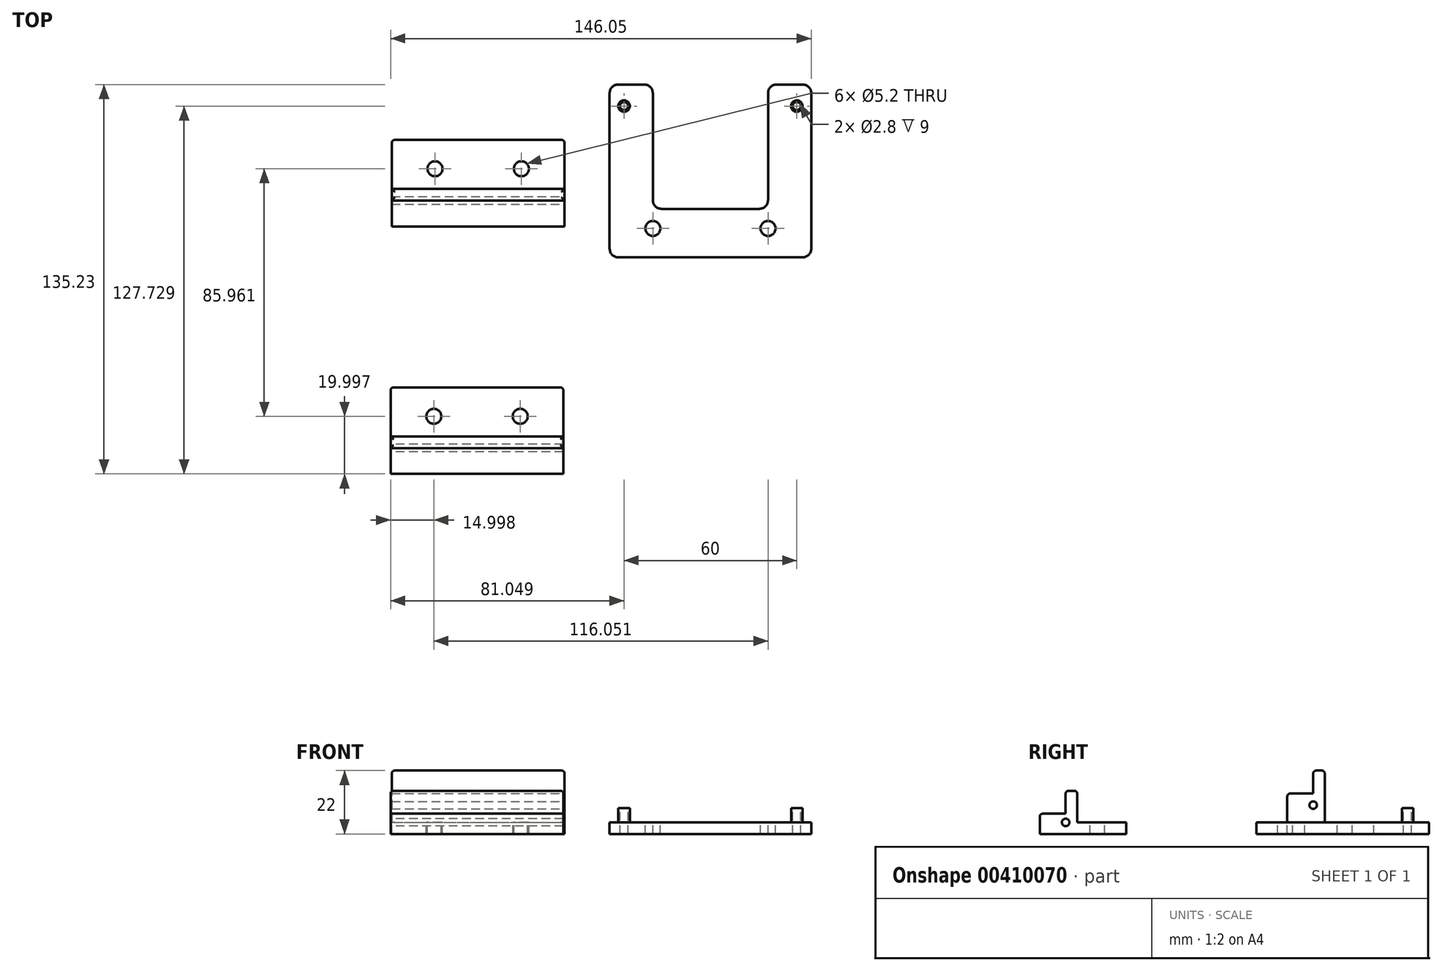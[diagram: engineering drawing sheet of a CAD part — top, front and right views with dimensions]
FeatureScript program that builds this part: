
annotation { "Feature Type Name" : "Feature", "Feature Type Description" : "" }
export const myFeature = defineFeature(function(context is Context, id is Id, definition is map)
    precondition{}
    {
        {
            var Q0;
            Q0=qCreatedBy(makeId("Top.planeOp"),FACE);
            var sketch = newSketch(context, id + "F0", { "sketchPlane" : qUnion([Q0])});
            skLineSegment(sketch, "E0.bottom", {"start": v(-70.8, 61.37) * mm, "end": v(-10.8, 61.37) * mm});
            skLineSegment(sketch, "E0.top", {"start": v(-70.8, 31.37) * mm, "end": v(-10.8, 31.37) * mm});
            skLineSegment(sketch, "E0.left", {"start": v(-70.8, 61.37) * mm, "end": v(-70.8, 31.37) * mm});
            skLineSegment(sketch, "E0.right", {"start": v(-10.8, 61.37) * mm, "end": v(-10.8, 31.37) * mm});
            skCircle(sketch, "E1", {"center": v(-55.8, 51.37) * mm, "radius": 2.6 * mm});
            skCircle(sketch, "E2", {"center": v(-25.8, 51.37) * mm, "radius": 2.6 * mm});
            skLineSegment(sketch, "E3", {"start": v(-70.8, 44.37) * mm, "end": v(-10.8, 44.37) * mm});
            skSolve(sketch);
        }
        {
            var Q0;
            Q0 = qSketchRegion(id + "F0", true);
            extrude(context, id + "F1", {"entities" : qUnion([Q0]), "depth" : -4 * mm});
        }
        {
            var Q0;
            {var subQ0=sQuery(id+"F0.wireOp",EDGE,"E0.top");Q0=makeQuery(id+"F0.imprint","IMPRINT",FACE,{"disambiguationData":[TD([[makeQuery(id+"F0.imprint","IMPRINT",EDGE,{"derivedFrom":subQ0}),1.0]])]});}
            extrude(context, id + "F2", {"entities" : qUnion([Q0]), "operationType" : NewBodyOperationType.ADD, "depth" : 10 * mm});
        }
        {
            var Q0;
            Q0=makeQuery(id+"F2.opExtrude","CAP_FACE",FACE,{"disambiguationData":[OSD([sQuery(id+"F0.wireOp",EDGE,"E0.top"),sQuery(id+"F0.wireOp",EDGE,"E0.left"),sQuery(id+"F0.wireOp",EDGE,"E0.right"),sQuery(id+"F0.wireOp",EDGE,"E3")])],"isStart":false});
            var sketch = newSketch(context, id + "F3", { "sketchPlane" : qUnion([Q0])});
            skLineSegment(sketch, "E4", {"start": v(-70.8, 40.37) * mm, "end": v(-10.8, 40.37) * mm});
            skSolve(sketch);
        }
        {
            var Q0;
            {var subQ0=sQuery(id+"F3.wireOp",EDGE,"E4");Q0=makeQuery(id+"F3.imprint","IMPRINT",FACE,{"disambiguationData":[TD([[makeQuery(id+"F3.imprint","IMPRINT",EDGE,{"derivedFrom":subQ0}),1.0]])]});}
            extrude(context, id + "F4", {"entities" : qUnion([Q0]), "operationType" : NewBodyOperationType.ADD, "depth" : 8 * mm});
        }
        {
            var Q0;
            {var subQ0=sQuery(id+"F0.wireOp",EDGE,"E0.right");Q0=makeQuery(id+"F4.boolean.opBoolean","MERGE",FACE,{"derivedFrom":[makeQuery(id+"F2.boolean.opBoolean","MERGE",FACE,{"derivedFrom":[makeQuery(id+"F1.opExtrude","SWEPT_FACE",FACE,{"disambiguationData":[OSD([subQ0])]}),makeQuery(id+"F2.opExtrude","SWEPT_FACE",FACE,{"disambiguationData":[OSD([subQ0])]})]}),makeQuery(id+"F4.opExtrude","SWEPT_FACE",FACE,{"disambiguationData":[OSD([subQ0])]})]});}
            var sketch = newSketch(context, id + "F5", { "sketchPlane" : qUnion([Q0])});
            skCircle(sketch, "E5", {"center": v(40.37, 6) * mm, "radius": 1.3 * mm});
            skSolve(sketch);
        }
        {
            var Q0;
            Q0=makeQuery(id+"F5.imprint","IMPRINT",FACE,{"disambiguationData":[TD([[makeQuery(id+"F5.imprint","IMPRINT",EDGE,{"derivedFrom":sQuery(id+"F5.wireOp",EDGE,"E5")}),1.0]])]});
            extrude(context, id + "F6", {"entities" : qUnion([Q0]), "operationType" : NewBodyOperationType.REMOVE, "endBound" : BoundingType.THROUGH_ALL, "oppositeDirection" : true, "depth" : 25 * mm});
        }
        {
            var Q0;
            Q0=makeQuery(id+"F2.opExtrude","CAP_EDGE",EDGE,{"disambiguationData":[OSD([sQuery(id+"F0.wireOp",EDGE,"E3")])],"isStart":true});
            var Q1;
            Q1=makeQuery(id+"F1.opExtrude","SWEPT_EDGE",EDGE,{"disambiguationData":[OSD([sQuery(id+"F0.wireOp",EDGE,"E0.bottom"),sQuery(id+"F0.wireOp",EDGE,"E0.left")])]});
            var Q2;
            Q2=makeQuery(id+"F1.opExtrude","SWEPT_EDGE",EDGE,{"disambiguationData":[OSD([sQuery(id+"F0.wireOp",EDGE,"E0.bottom"),sQuery(id+"F0.wireOp",EDGE,"E0.right")])]});
            var Q3;
            Q3=makeQuery(id+"F4.opExtrude","CAP_EDGE",EDGE,{"disambiguationData":[OSD([sQuery(id+"F0.wireOp",EDGE,"E0.right")])],"isStart":false});
            var Q4;
            Q4=makeQuery(id+"F4.opExtrude","CAP_EDGE",EDGE,{"disambiguationData":[OSD([sQuery(id+"F0.wireOp",EDGE,"E0.left")])],"isStart":false});
            var Q5;
            Q5=makeQuery(id+"F4.opExtrude","CAP_EDGE",EDGE,{"disambiguationData":[OSD([sQuery(id+"F3.wireOp",EDGE,"E4")])],"isStart":false});
            var Q6;
            Q6=makeQuery(id+"F4.opExtrude","CAP_EDGE",EDGE,{"disambiguationData":[OSD([sQuery(id+"F0.wireOp",EDGE,"E3")])],"isStart":false});
            var Q7;
            Q7=makeQuery(id+"F2.opExtrude","CAP_EDGE",EDGE,{"disambiguationData":[OSD([sQuery(id+"F0.wireOp",EDGE,"E0.top")])],"isStart":false});
            fillet(context, id + "F7", {"entities" : qUnion([Q0, Q1, Q2, Q3, Q4, Q5, Q6, Q7]), "radius" : 1 * mm, "tangentPropagation" : true, "allowEdgeOverflow" : false});
        }
        {
            var Q0;
            Q0=qCreatedBy(makeId("Top.planeOp"),FACE);
            var sketch = newSketch(context, id + "F8", { "sketchPlane" : qUnion([Q0])});
            skLineSegment(sketch, "E6.bottom", {"start": v(-71.2, -24.6) * mm, "end": v(-11.2, -24.6) * mm});
            skLineSegment(sketch, "E6.top", {"start": v(-71.2, -54.6) * mm, "end": v(-11.2, -54.6) * mm});
            skLineSegment(sketch, "E6.left", {"start": v(-71.2, -24.6) * mm, "end": v(-71.2, -54.6) * mm});
            skLineSegment(sketch, "E6.right", {"start": v(-11.2, -24.6) * mm, "end": v(-11.2, -54.6) * mm});
            skCircle(sketch, "E7", {"center": v(-56.2, -34.6) * mm, "radius": 2.6 * mm});
            skCircle(sketch, "E8", {"center": v(-26.2, -34.6) * mm, "radius": 2.6 * mm});
            skLineSegment(sketch, "E9", {"start": v(-71.2, -41.6) * mm, "end": v(-11.2, -41.6) * mm});
            skSolve(sketch);
        }
        {
            var Q0;
            {var subQ0=sQuery(id+"F8.wireOp",EDGE,"E6.top");Q0=makeQuery(id+"F8.imprint","IMPRINT",FACE,{"disambiguationData":[TD([[makeQuery(id+"F8.imprint","IMPRINT",EDGE,{"derivedFrom":subQ0}),1.0]])]});}
            var Q1;
            {var subQ1=sQuery(id+"F8.wireOp",EDGE,"E6.bottom");Q1=makeQuery(id+"F8.imprint","IMPRINT",FACE,{"disambiguationData":[TD([[makeQuery(id+"F8.imprint","IMPRINT",EDGE,{"derivedFrom":subQ1}),-1.0]])]});}
            extrude(context, id + "F9", {"entities" : qUnion([Q0, Q1]), "oppositeDirection" : true, "depth" : 4 * mm});
        }
        {
            var Q0;
            {var subQ0=sQuery(id+"F8.wireOp",EDGE,"E6.top");Q0=makeQuery(id+"F8.imprint","IMPRINT",FACE,{"disambiguationData":[TD([[makeQuery(id+"F8.imprint","IMPRINT",EDGE,{"derivedFrom":subQ0}),1.0]])]});}
            extrude(context, id + "F10", {"entities" : qUnion([Q0]), "operationType" : NewBodyOperationType.ADD, "depth" : 3 * mm});
        }
        {
            var Q0;
            Q0=makeQuery(id+"F10.opExtrude","CAP_FACE",FACE,{"disambiguationData":[OSD([sQuery(id+"F8.wireOp",EDGE,"E6.top"),sQuery(id+"F8.wireOp",EDGE,"E6.left"),sQuery(id+"F8.wireOp",EDGE,"E6.right"),sQuery(id+"F8.wireOp",EDGE,"E9")])],"isStart":false});
            var sketch = newSketch(context, id + "F11", { "sketchPlane" : qUnion([Q0])});
            skLineSegment(sketch, "E10", {"start": v(-71.2, -45.6) * mm, "end": v(-11.2, -45.6) * mm});
            skSolve(sketch);
        }
        {
            var Q0;
            {var subQ0=sQuery(id+"F11.wireOp",EDGE,"E10");Q0=makeQuery(id+"F11.imprint","IMPRINT",FACE,{"disambiguationData":[TD([[makeQuery(id+"F11.imprint","IMPRINT",EDGE,{"derivedFrom":subQ0}),1.0]])]});}
            extrude(context, id + "F12", {"entities" : qUnion([Q0]), "operationType" : NewBodyOperationType.ADD, "depth" : 8 * mm});
        }
        {
            var Q0;
            {var subQ0=sQuery(id+"F8.wireOp",EDGE,"E6.left");Q0=makeQuery(id+"F12.boolean.opBoolean","MERGE",FACE,{"derivedFrom":[makeQuery(id+"F10.boolean.opBoolean","MERGE",FACE,{"derivedFrom":[makeQuery(id+"F9.opExtrude","SWEPT_FACE",FACE,{"disambiguationData":[OSD([subQ0])]}),makeQuery(id+"F10.opExtrude","SWEPT_FACE",FACE,{"disambiguationData":[OSD([subQ0])]})]}),makeQuery(id+"F12.opExtrude","SWEPT_FACE",FACE,{"disambiguationData":[OSD([subQ0])]})]});}
            var sketch = newSketch(context, id + "F13", { "sketchPlane" : qUnion([Q0])});
            skCircle(sketch, "E11", {"center": v(45.6, 0) * mm, "radius": 1.3 * mm});
            skSolve(sketch);
        }
        {
            var Q0;
            Q0=makeQuery(id+"F13.imprint","IMPRINT",FACE,{"disambiguationData":[TD([[makeQuery(id+"F13.imprint","IMPRINT",EDGE,{"derivedFrom":sQuery(id+"F13.wireOp",EDGE,"E11")}),1.0]])]});
            extrude(context, id + "F14", {"entities" : qUnion([Q0]), "operationType" : NewBodyOperationType.REMOVE, "endBound" : BoundingType.THROUGH_ALL, "oppositeDirection" : true, "depth" : 25 * mm});
        }
        {
            var Q0;
            Q0=makeQuery(id+"F10.opExtrude","CAP_EDGE",EDGE,{"disambiguationData":[OSD([sQuery(id+"F8.wireOp",EDGE,"E9")])],"isStart":true});
            var Q1;
            Q1=makeQuery(id+"F9.opExtrude","SWEPT_EDGE",EDGE,{"disambiguationData":[OSD([sQuery(id+"F8.wireOp",EDGE,"E6.bottom"),sQuery(id+"F8.wireOp",EDGE,"E6.left")])]});
            var Q2;
            Q2=makeQuery(id+"F9.opExtrude","SWEPT_EDGE",EDGE,{"disambiguationData":[OSD([sQuery(id+"F8.wireOp",EDGE,"E6.bottom"),sQuery(id+"F8.wireOp",EDGE,"E6.right")])]});
            var Q3;
            Q3=makeQuery(id+"F12.opExtrude","CAP_EDGE",EDGE,{"disambiguationData":[OSD([sQuery(id+"F8.wireOp",EDGE,"E6.right")])],"isStart":false});
            var Q4;
            Q4=makeQuery(id+"F12.opExtrude","CAP_EDGE",EDGE,{"disambiguationData":[OSD([sQuery(id+"F8.wireOp",EDGE,"E6.left")])],"isStart":false});
            var Q5;
            Q5=makeQuery(id+"F12.opExtrude","CAP_EDGE",EDGE,{"disambiguationData":[OSD([sQuery(id+"F11.wireOp",EDGE,"E10")])],"isStart":false});
            var Q6;
            Q6=makeQuery(id+"F12.opExtrude","CAP_EDGE",EDGE,{"disambiguationData":[OSD([sQuery(id+"F8.wireOp",EDGE,"E9")])],"isStart":false});
            var Q7;
            Q7=makeQuery(id+"F10.opExtrude","CAP_EDGE",EDGE,{"disambiguationData":[OSD([sQuery(id+"F8.wireOp",EDGE,"E6.top")])],"isStart":false});
            fillet(context, id + "F15", {"entities" : qUnion([Q0, Q1, Q2, Q3, Q4, Q5, Q6, Q7]), "radius" : 1 * mm, "tangentPropagation" : true, "allowEdgeOverflow" : false});
        }
        {
            var Q0;
            Q0=qCreatedBy(makeId("Top.planeOp"),FACE);
            var sketch = newSketch(context, id + "F16", { "sketchPlane" : qUnion([Q0])});
            skLineSegment(sketch, "E12.bottom", {"start": v(4.85, 80.64) * mm, "end": v(19.85, 80.64) * mm});
            skLineSegment(sketch, "E12.top", {"start": v(4.85, 20.64) * mm, "end": v(74.85, 20.64) * mm});
            skLineSegment(sketch, "E12.left", {"start": v(4.85, 80.64) * mm, "end": v(4.85, 20.64) * mm});
            skLineSegment(sketch, "E12.right", {"start": v(74.85, 80.64) * mm, "end": v(74.85, 20.64) * mm});
            skCircle(sketch, "E13", {"center": v(9.85, 73.14) * mm, "radius": 1.4 * mm});
            skCircle(sketch, "E14", {"center": v(69.85, 73.14) * mm, "radius": 1.4 * mm});
            skLineSegment(sketch, "E15.top", {"start": v(19.85, 37.46) * mm, "end": v(59.85, 37.46) * mm});
            skLineSegment(sketch, "E15.left", {"start": v(19.85, 80.64) * mm, "end": v(19.85, 37.46) * mm});
            skLineSegment(sketch, "E15.right", {"start": v(59.85, 80.64) * mm, "end": v(59.85, 37.46) * mm});
            skLineSegment(sketch, "E16.trimOffspring", {"start": v(59.85, 80.64) * mm, "end": v(74.85, 80.64) * mm});
            skCircle(sketch, "E17", {"center": v(9.85, 73.14) * mm, "radius": 2 * mm});
            skCircle(sketch, "E18", {"center": v(69.85, 73.14) * mm, "radius": 2 * mm});
            skCircle(sketch, "E19", {"center": v(19.85, 30.64) * mm, "radius": 2.6 * mm});
            skCircle(sketch, "E20", {"center": v(59.85, 30.64) * mm, "radius": 2.6 * mm});
            skSolve(sketch);
        }
        {
            var Q0;
            Q0 = qSketchRegion(id + "F16", true);
            var Q1;
            Q1=makeQuery(id+"F16.imprint","IMPRINT",FACE,{"disambiguationData":[TD([[makeQuery(id+"F16.imprint","IMPRINT",EDGE,{"derivedFrom":sQuery(id+"F16.wireOp",EDGE,"E13")}),-1.0]])]});
            var Q2;
            Q2=makeQuery(id+"F16.imprint","IMPRINT",FACE,{"disambiguationData":[TD([[makeQuery(id+"F16.imprint","IMPRINT",EDGE,{"derivedFrom":sQuery(id+"F16.wireOp",EDGE,"E14")}),-1.0]])]});
            extrude(context, id + "F17", {"entities" : qUnion([Q0, Q1, Q2]), "oppositeDirection" : true, "depth" : 4 * mm});
        }
        {
            var Q0;
            Q0=makeQuery(id+"F16.imprint","IMPRINT",FACE,{"disambiguationData":[TD([[makeQuery(id+"F16.imprint","IMPRINT",EDGE,{"derivedFrom":sQuery(id+"F16.wireOp",EDGE,"E14")}),-1.0]])]});
            var Q1;
            Q1=makeQuery(id+"F16.imprint","IMPRINT",FACE,{"disambiguationData":[TD([[makeQuery(id+"F16.imprint","IMPRINT",EDGE,{"derivedFrom":sQuery(id+"F16.wireOp",EDGE,"E13")}),-1.0]])]});
            extrude(context, id + "F18", {"entities" : qUnion([Q0, Q1]), "operationType" : NewBodyOperationType.ADD, "depth" : 5 * mm});
        }
        {
            var Q0;
            Q0=makeQuery(id+"F17.opExtrude","SWEPT_EDGE",EDGE,{"disambiguationData":[OSD([sQuery(id+"F16.wireOp",EDGE,"E12.bottom"),sQuery(id+"F16.wireOp",EDGE,"E12.left")])]});
            var Q1;
            Q1=makeQuery(id+"F17.opExtrude","SWEPT_EDGE",EDGE,{"disambiguationData":[OSD([sQuery(id+"F16.wireOp",EDGE,"E12.bottom"),sQuery(id+"F16.wireOp",EDGE,"E15.left")])]});
            var Q2;
            Q2=makeQuery(id+"F17.opExtrude","SWEPT_EDGE",EDGE,{"disambiguationData":[OSD([sQuery(id+"F16.wireOp",EDGE,"E15.right"),sQuery(id+"F16.wireOp",EDGE,"E16.trimOffspring")])]});
            var Q3;
            Q3=makeQuery(id+"F17.opExtrude","SWEPT_EDGE",EDGE,{"disambiguationData":[OSD([sQuery(id+"F16.wireOp",EDGE,"E12.right"),sQuery(id+"F16.wireOp",EDGE,"E16.trimOffspring")])]});
            var Q4;
            Q4=makeQuery(id+"F17.opExtrude","SWEPT_EDGE",EDGE,{"disambiguationData":[OSD([sQuery(id+"F16.wireOp",EDGE,"E15.top"),sQuery(id+"F16.wireOp",EDGE,"E15.left")])]});
            var Q5;
            Q5=makeQuery(id+"F17.opExtrude","SWEPT_EDGE",EDGE,{"disambiguationData":[OSD([sQuery(id+"F16.wireOp",EDGE,"E15.top"),sQuery(id+"F16.wireOp",EDGE,"E15.right")])]});
            var Q6;
            Q6=makeQuery(id+"F17.opExtrude","SWEPT_EDGE",EDGE,{"disambiguationData":[OSD([sQuery(id+"F16.wireOp",EDGE,"E12.top"),sQuery(id+"F16.wireOp",EDGE,"E12.left")])]});
            var Q7;
            Q7=makeQuery(id+"F17.opExtrude","SWEPT_EDGE",EDGE,{"disambiguationData":[OSD([sQuery(id+"F16.wireOp",EDGE,"E12.top"),sQuery(id+"F16.wireOp",EDGE,"E12.right")])]});
            var Q8;
            Q8=makeQuery(id+"F18.opExtrude","CAP_EDGE",EDGE,{"disambiguationData":[OSD([sQuery(id+"F16.wireOp",EDGE,"E17")])],"isStart":true});
            var Q9;
            Q9=makeQuery(id+"F18.opExtrude","CAP_EDGE",EDGE,{"disambiguationData":[OSD([sQuery(id+"F16.wireOp",EDGE,"E18")])],"isStart":true});
            fillet(context, id + "F19", {"entities" : qUnion([Q0, Q1, Q2, Q3, Q4, Q5, Q6, Q7, Q8, Q9]), "radius" : 3 * mm, "tangentPropagation" : true, "allowEdgeOverflow" : false});
        }
    });
